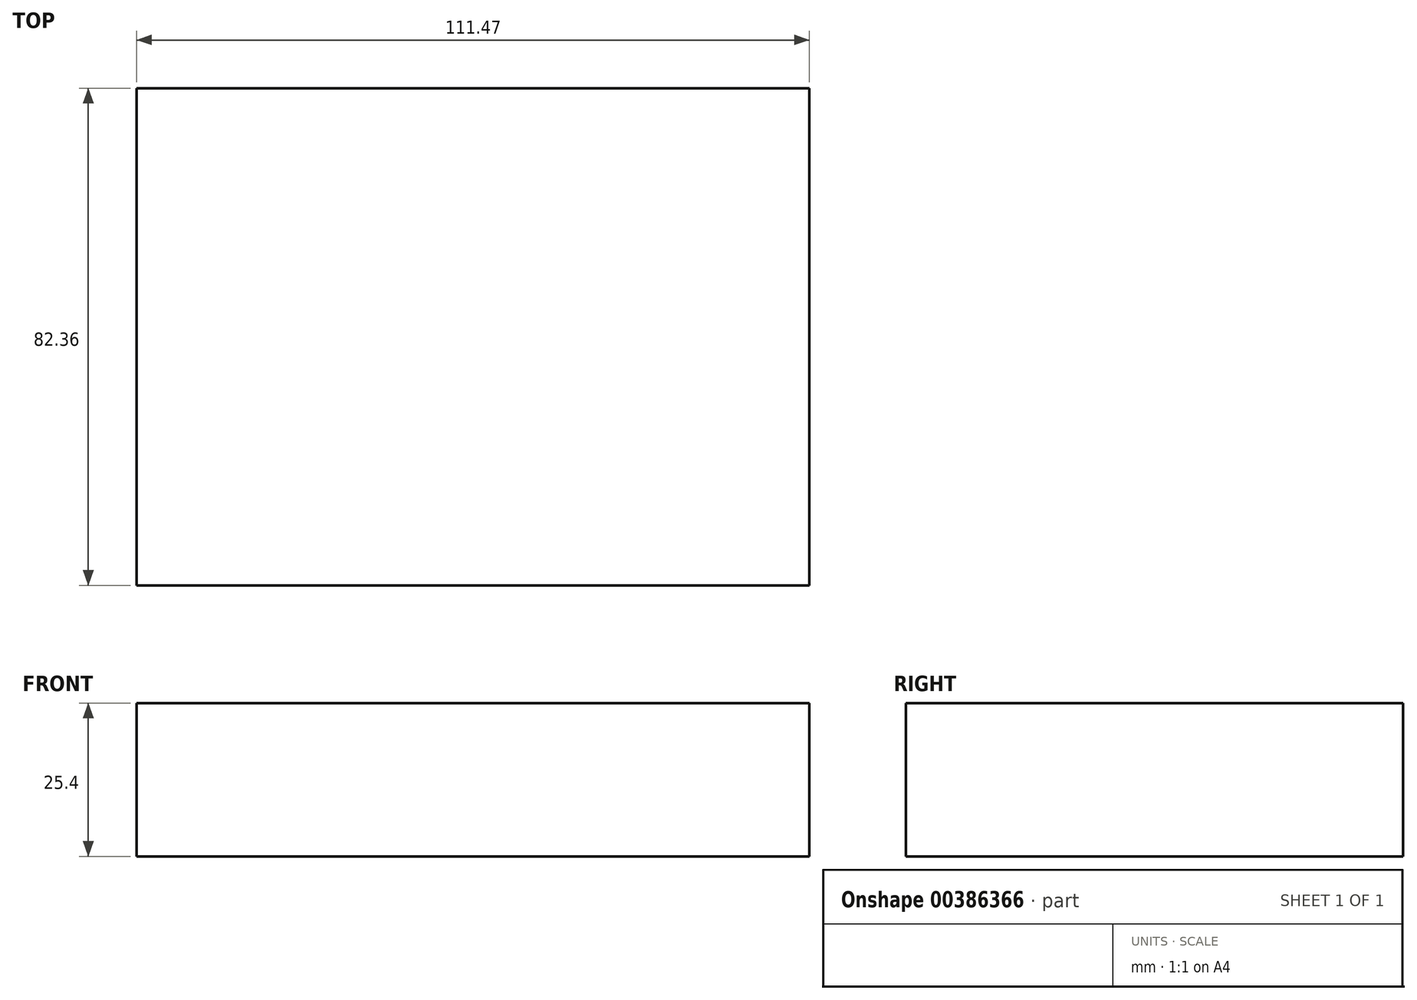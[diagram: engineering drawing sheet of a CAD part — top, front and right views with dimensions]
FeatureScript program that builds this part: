
annotation { "Feature Type Name" : "Feature", "Feature Type Description" : "" }
export const myFeature = defineFeature(function(context is Context, id is Id, definition is map)
    precondition{}
    {
        {
            var Q0;
            Q0=qCreatedBy(makeId("Top.planeOp"),FACE);
            var sketch = newSketch(context, id + "F0", { "sketchPlane" : qUnion([Q0])});
            skLineSegment(sketch, "E0.bottom", {"start": v(-65.32, -36.71) * mm, "end": v(46.15, -36.71) * mm});
            skLineSegment(sketch, "E0.top", {"start": v(-65.32, 45.65) * mm, "end": v(46.15, 45.65) * mm});
            skLineSegment(sketch, "E0.left", {"start": v(-65.32, -36.71) * mm, "end": v(-65.32, 45.65) * mm});
            skLineSegment(sketch, "E0.right", {"start": v(46.15, -36.71) * mm, "end": v(46.15, 45.65) * mm});
            skSolve(sketch);
        }
        {
            var Q0;
            Q0=makeQuery(id+"F0.imprint","IMPRINT",FACE,{"disambiguationData":[TD([[makeQuery(id+"F0.imprint","IMPRINT",EDGE,{"derivedFrom":sQuery(id+"F0.wireOp",EDGE,"E0.bottom")}),1.0]])]});
            extrude(context, id + "F1", {"entities" : qUnion([Q0]), "depth" : 25.4 * mm});
        }
    });
